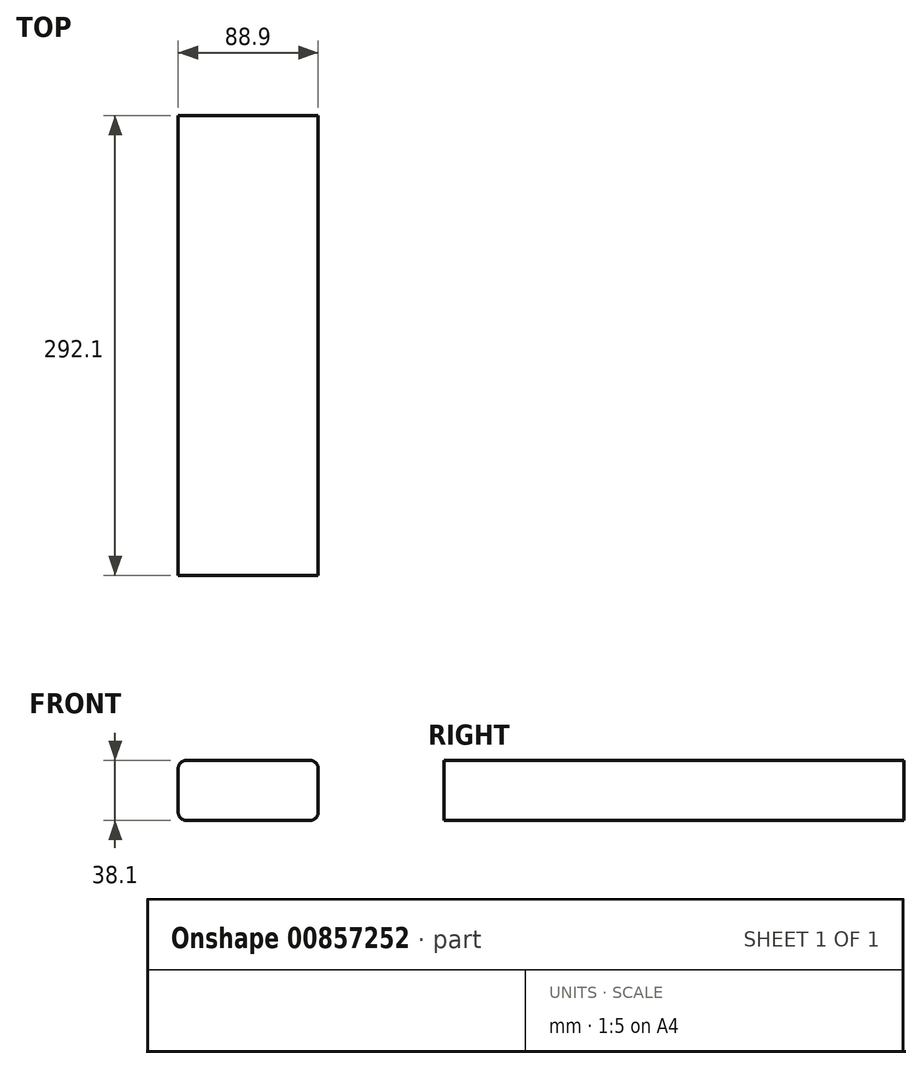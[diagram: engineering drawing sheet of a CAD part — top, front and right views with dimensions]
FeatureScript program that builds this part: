
annotation { "Feature Type Name" : "Feature", "Feature Type Description" : "" }
export const myFeature = defineFeature(function(context is Context, id is Id, definition is map)
    precondition{}
    {
        {
            var Q0;
            Q0=qCreatedBy(makeId("Top.planeOp"),FACE);
            var sketch = newSketch(context, id + "F0", { "sketchPlane" : qUnion([Q0])});
            skLineSegment(sketch, "E0.bottom", {"start": v(-74.4, 245.83) * mm, "end": v(14.5, 245.83) * mm});
            skLineSegment(sketch, "E0.top", {"start": v(-74.4, -46.27) * mm, "end": v(14.5, -46.27) * mm});
            skLineSegment(sketch, "E0.left", {"start": v(-74.4, 245.83) * mm, "end": v(-74.4, -46.27) * mm});
            skLineSegment(sketch, "E0.right", {"start": v(14.5, 245.83) * mm, "end": v(14.5, -46.27) * mm});
            skSolve(sketch);
        }
        {
            var Q0;
            Q0=makeQuery(id+"F0.imprint","IMPRINT",FACE,{"disambiguationData":[TD([[makeQuery(id+"F0.imprint","IMPRINT",EDGE,{"derivedFrom":sQuery(id+"F0.wireOp",EDGE,"E0.bottom")}),-1.0]])]});
            extrude(context, id + "F1", {"entities" : qUnion([Q0]), "depth" : 38.1 * mm, "offsetDistance" : 25.4 * mm});
        }
        {
            var Q0;
            Q0=makeQuery(id+"F1.opExtrude","CAP_EDGE",EDGE,{"disambiguationData":[OSD([sQuery(id+"F0.wireOp",EDGE,"E0.right")])],"isStart":false});
            fillet(context, id + "F2", {"entities" : qUnion([Q0]), "radius" : 5.08 * mm, "tangentPropagation" : true, "allowEdgeOverflow" : false});
        }
        {
            var Q0;
            Q0=makeQuery(id+"F1.opExtrude","CAP_EDGE",EDGE,{"disambiguationData":[OSD([sQuery(id+"F0.wireOp",EDGE,"E0.left")])],"isStart":false});
            var Q1;
            Q1=makeQuery(id+"F1.opExtrude","CAP_EDGE",EDGE,{"disambiguationData":[OSD([sQuery(id+"F0.wireOp",EDGE,"E0.right")])],"isStart":true});
            var Q2;
            Q2=makeQuery(id+"F1.opExtrude","CAP_EDGE",EDGE,{"disambiguationData":[OSD([sQuery(id+"F0.wireOp",EDGE,"E0.left")])],"isStart":true});
            fillet(context, id + "F3", {"entities" : qUnion([Q0, Q1, Q2]), "radius" : 5.08 * mm, "tangentPropagation" : true, "allowEdgeOverflow" : false});
        }
    });
